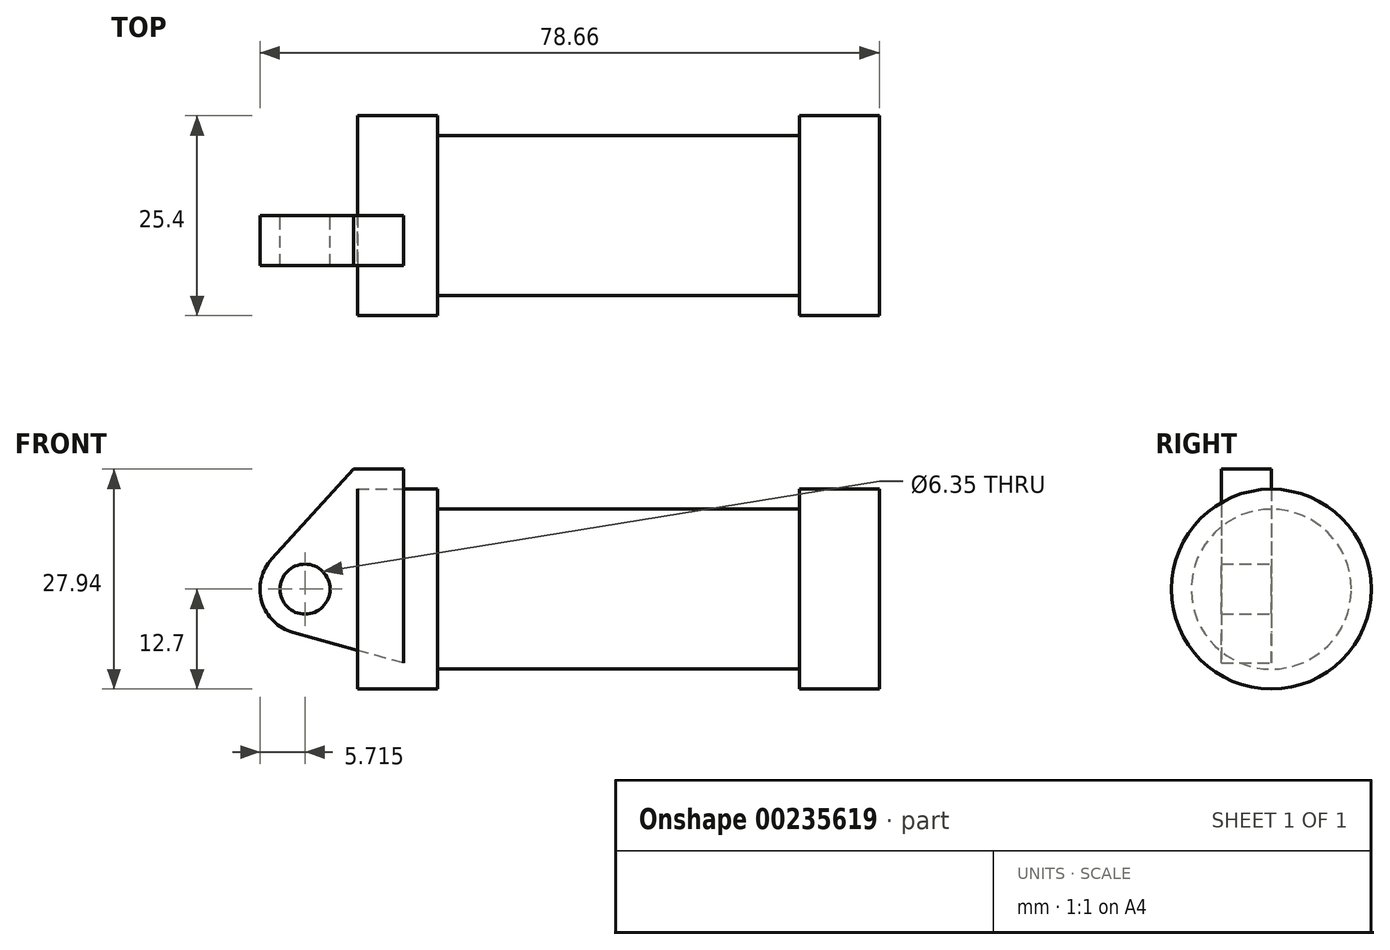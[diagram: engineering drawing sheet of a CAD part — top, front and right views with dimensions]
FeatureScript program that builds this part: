
annotation { "Feature Type Name" : "Feature", "Feature Type Description" : "" }
export const myFeature = defineFeature(function(context is Context, id is Id, definition is map)
    precondition{}
    {
        {
            var Q0;
            Q0=qCreatedBy(makeId("Front.planeOp"),FACE);
            var sketch = newSketch(context, id + "F0", { "sketchPlane" : qUnion([Q0])});
            skLineSegment(sketch, "E0", {"start": v(0, 0) * mm, "end": v(0, 12.7) * mm});
            skLineSegment(sketch, "E1", {"start": v(0, 12.7) * mm, "end": v(10.16, 12.7) * mm});
            skLineSegment(sketch, "E2", {"start": v(10.16, 12.7) * mm, "end": v(10.16, 10.16) * mm});
            skLineSegment(sketch, "E3", {"start": v(10.16, 10.16) * mm, "end": v(56.13, 10.16) * mm});
            skLineSegment(sketch, "E4", {"start": v(56.13, 10.16) * mm, "end": v(56.13, 12.7) * mm});
            skLineSegment(sketch, "E5", {"start": v(56.13, 12.7) * mm, "end": v(66.3, 12.7) * mm});
            skLineSegment(sketch, "E6", {"start": v(66.3, 12.7) * mm, "end": v(66.3, 0) * mm});
            skLineSegment(sketch, "E7", {"start": v(66.3, 0) * mm, "end": v(0, 0) * mm});
            skLineSegment(sketch, "E8", {"start": v(5.84, 15.24) * mm, "end": v(-0.5, 15.24) * mm});
            skLineSegment(sketch, "E9", {"start": v(-0.5, 15.24) * mm, "end": v(-10.88, 3.85) * mm});
            skLineSegment(sketch, "E10", {"start": v(0, 0) * mm, "end": v(-6.65, 0) * mm});
            skCircle(sketch, "E11", {"center": v(-6.65, 0) * mm, "radius": 5.72 * mm});
            skCircle(sketch, "E12", {"center": v(-6.65, 0) * mm, "radius": 3.18 * mm});
            skLineSegment(sketch, "E13", {"start": v(5.84, 15.24) * mm, "end": v(5.84, -9.4) * mm});
            skLineSegment(sketch, "E14", {"start": v(5.84, -9.4) * mm, "end": v(-8.18, -5.5) * mm});
            skSolve(sketch);
        }
        {
            var Q0;
            {var subQ0=sQuery(id+"F0.wireOp",EDGE,"E2");Q0=makeQuery(id+"F0.imprint","IMPRINT",FACE,{"disambiguationData":[TD([[makeQuery(id+"F0.imprint","IMPRINT",EDGE,{"derivedFrom":subQ0}),-1.0]])]});}
            var Q1;
            {var subQ0=sQuery(id+"F0.wireOp",EDGE,"E0");Q1=makeQuery(id+"F0.imprint","IMPRINT",FACE,{"disambiguationData":[TD([[makeQuery(id+"F0.imprint","IMPRINT",EDGE,{"derivedFrom":subQ0}),-1.0]])]});}
            var Q2;
            Q2=sQuery(id+"F0.wireOp",EDGE,"E7");
            revolve(context, id + "F1", {"entities" : qUnion([Q0, Q1]), "axis" : qUnion([Q2]), "revolveType" : RevolveType.FULL});
        }
        {
            var Q0;
            {var subQ3=sQuery(id+"F0.wireOp",EDGE,"E0");Q0=makeQuery(id+"F0.imprint","IMPRINT",FACE,{"disambiguationData":[TD([[makeQuery(id+"F0.imprint","IMPRINT",EDGE,{"derivedFrom":subQ3}),1.0]])]});}
            var Q1;
            {var subQ0=sQuery(id+"F0.wireOp",EDGE,"E0");Q1=makeQuery(id+"F0.imprint","IMPRINT",FACE,{"disambiguationData":[TD([[makeQuery(id+"F0.imprint","IMPRINT",EDGE,{"derivedFrom":subQ0}),-1.0]])]});}
            var Q2;
            {var subQ0=sQuery(id+"F0.wireOp",EDGE,"E14");Q2=makeQuery(id+"F0.imprint","IMPRINT",FACE,{"disambiguationData":[TD([[makeQuery(id+"F0.imprint","IMPRINT",EDGE,{"derivedFrom":subQ0}),-1.0]])]});}
            var Q3;
            {var subQ4=sQuery(id+"F0.wireOp",EDGE,"E12");Q3=makeQuery(id+"F0.imprint","IMPRINT",FACE,{"disambiguationData":[TD([[makeQuery(id+"F0.imprint","IMPRINT",EDGE,{"derivedFrom":subQ4}),-1.0]])]});}
            extrude(context, id + "F2", {"entities" : qUnion([Q0, Q1, Q2, Q3]), "depth" : 6.35 * mm});
        }
    });
